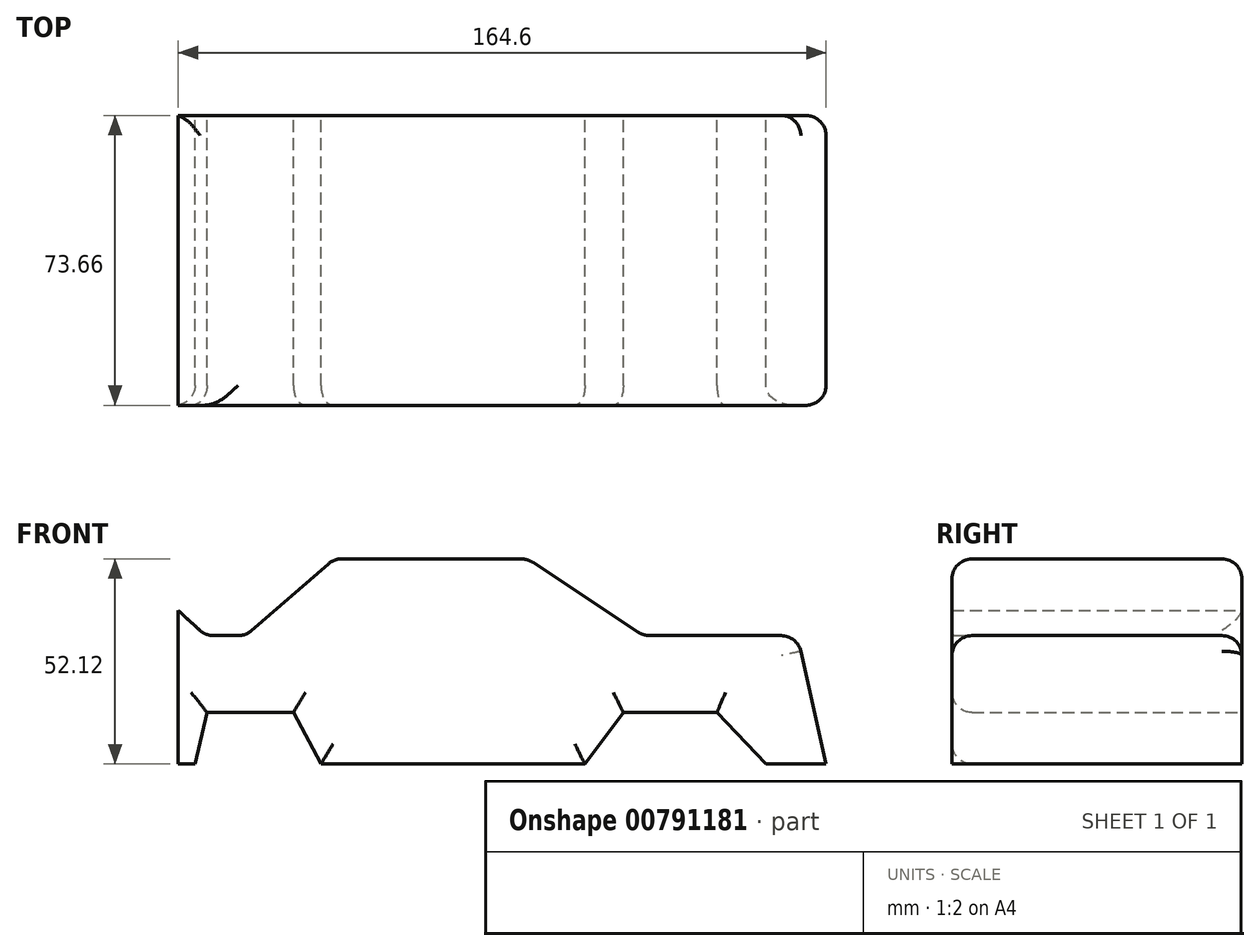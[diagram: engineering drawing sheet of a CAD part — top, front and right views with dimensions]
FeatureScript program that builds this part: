
annotation { "Feature Type Name" : "Feature", "Feature Type Description" : "" }
export const myFeature = defineFeature(function(context is Context, id is Id, definition is map)
    precondition{}
    {
        {
            var Q0;
            Q0=qCreatedBy(makeId("Front.planeOp"),FACE);
            var sketch = newSketch(context, id + "F0", { "sketchPlane" : qUnion([Q0])});
            skLineSegment(sketch, "E0", {"start": v(-94.95, -16.46) * mm, "end": v(-94.95, 22.56) * mm});
            skLineSegment(sketch, "E1", {"start": v(-94.95, 22.56) * mm, "end": v(-87.93, 16.15) * mm});
            skLineSegment(sketch, "E2", {"start": v(-87.93, 16.15) * mm, "end": v(-77.88, 16.15) * mm});
            skLineSegment(sketch, "E3", {"start": v(-77.88, 16.15) * mm, "end": v(-55.32, 35.66) * mm});
            skLineSegment(sketch, "E4", {"start": v(-6.25, 35.66) * mm, "end": v(-55.32, 35.66) * mm});
            skLineSegment(sketch, "E5", {"start": v(-6.25, 35.66) * mm, "end": v(23.32, 16.15) * mm});
            skLineSegment(sketch, "E6", {"start": v(23.32, 16.15) * mm, "end": v(62.33, 16.15) * mm});
            skLineSegment(sketch, "E7", {"start": v(62.33, 16.15) * mm, "end": v(69.65, -16.46) * mm});
            skLineSegment(sketch, "E8", {"start": v(69.65, -16.46) * mm, "end": v(54.4, -16.46) * mm});
            skLineSegment(sketch, "E9", {"start": v(54.4, -16.46) * mm, "end": v(41.91, -3.35) * mm});
            skLineSegment(sketch, "E10", {"start": v(18.14, -3.35) * mm, "end": v(41.91, -3.35) * mm});
            skLineSegment(sketch, "E11", {"start": v(18.14, -3.35) * mm, "end": v(8.38, -16.46) * mm});
            skLineSegment(sketch, "E12", {"start": v(8.38, -16.46) * mm, "end": v(-58.67, -16.46) * mm});
            skLineSegment(sketch, "E13", {"start": v(-58.67, -16.46) * mm, "end": v(-65.68, -3.35) * mm});
            skLineSegment(sketch, "E14", {"start": v(-87.63, -3.35) * mm, "end": v(-65.68, -3.35) * mm});
            skLineSegment(sketch, "E15", {"start": v(-87.63, -3.35) * mm, "end": v(-90.68, -16.46) * mm});
            skLineSegment(sketch, "E16", {"start": v(-90.68, -16.46) * mm, "end": v(-94.95, -16.46) * mm});
            skSolve(sketch);
        }
        {
            var Q0;
            Q0=makeQuery(id+"F0.imprint","IMPRINT",FACE,{"disambiguationData":[TD([[makeQuery(id+"F0.imprint","IMPRINT",EDGE,{"derivedFrom":sQuery(id+"F0.wireOp",EDGE,"E0")}),-1.0]])]});
            extrude(context, id + "F1", {"entities" : qUnion([Q0]), "depth" : 73.66 * mm, "offsetDistance" : 25.4 * mm});
        }
        {
            var Q0;
            Q0=makeQuery(id+"F1.opExtrude","CAP_EDGE",EDGE,{"disambiguationData":[OSD([sQuery(id+"F0.wireOp",EDGE,"E7")])],"isStart":true});
            var Q1;
            Q1=makeQuery(id+"F1.opExtrude","SWEPT_EDGE",EDGE,{"disambiguationData":[OSD([sQuery(id+"F0.wireOp",EDGE,"E6"),sQuery(id+"F0.wireOp",EDGE,"E7")])]});
            var Q2;
            Q2=makeQuery(id+"F1.opExtrude","CAP_EDGE",EDGE,{"disambiguationData":[OSD([sQuery(id+"F0.wireOp",EDGE,"E7")])],"isStart":false});
            var Q3;
            Q3=makeQuery(id+"F1.opExtrude","CAP_EDGE",EDGE,{"disambiguationData":[OSD([sQuery(id+"F0.wireOp",EDGE,"E6")])],"isStart":true});
            var Q4;
            Q4=makeQuery(id+"F1.opExtrude","CAP_EDGE",EDGE,{"disambiguationData":[OSD([sQuery(id+"F0.wireOp",EDGE,"E5")])],"isStart":true});
            var Q5;
            Q5=makeQuery(id+"F1.opExtrude","SWEPT_EDGE",EDGE,{"disambiguationData":[OSD([sQuery(id+"F0.wireOp",EDGE,"E4"),sQuery(id+"F0.wireOp",EDGE,"E5")])]});
            var Q6;
            Q6=makeQuery(id+"F1.opExtrude","CAP_EDGE",EDGE,{"disambiguationData":[OSD([sQuery(id+"F0.wireOp",EDGE,"E5")])],"isStart":false});
            var Q7;
            Q7=makeQuery(id+"F1.opExtrude","CAP_EDGE",EDGE,{"disambiguationData":[OSD([sQuery(id+"F0.wireOp",EDGE,"E6")])],"isStart":false});
            var Q8;
            Q8=makeQuery(id+"F1.opExtrude","SWEPT_EDGE",EDGE,{"disambiguationData":[OSD([sQuery(id+"F0.wireOp",EDGE,"E5"),sQuery(id+"F0.wireOp",EDGE,"E6")])]});
            var Q9;
            Q9=makeQuery(id+"F1.opExtrude","CAP_EDGE",EDGE,{"disambiguationData":[OSD([sQuery(id+"F0.wireOp",EDGE,"E4")])],"isStart":true});
            var Q10;
            Q10=makeQuery(id+"F1.opExtrude","SWEPT_EDGE",EDGE,{"disambiguationData":[OSD([sQuery(id+"F0.wireOp",EDGE,"E3"),sQuery(id+"F0.wireOp",EDGE,"E4")])]});
            var Q11;
            Q11=makeQuery(id+"F1.opExtrude","CAP_EDGE",EDGE,{"disambiguationData":[OSD([sQuery(id+"F0.wireOp",EDGE,"E4")])],"isStart":false});
            var Q12;
            Q12=makeQuery(id+"F1.opExtrude","CAP_EDGE",EDGE,{"disambiguationData":[OSD([sQuery(id+"F0.wireOp",EDGE,"E3")])],"isStart":false});
            var Q13;
            Q13=makeQuery(id+"F1.opExtrude","SWEPT_EDGE",EDGE,{"disambiguationData":[OSD([sQuery(id+"F0.wireOp",EDGE,"E2"),sQuery(id+"F0.wireOp",EDGE,"E3")])]});
            var Q14;
            Q14=makeQuery(id+"F1.opExtrude","CAP_EDGE",EDGE,{"disambiguationData":[OSD([sQuery(id+"F0.wireOp",EDGE,"E3")])],"isStart":true});
            var Q15;
            Q15=makeQuery(id+"F1.opExtrude","CAP_EDGE",EDGE,{"disambiguationData":[OSD([sQuery(id+"F0.wireOp",EDGE,"E2")])],"isStart":true});
            var Q16;
            Q16=makeQuery(id+"F1.opExtrude","SWEPT_EDGE",EDGE,{"disambiguationData":[OSD([sQuery(id+"F0.wireOp",EDGE,"E1"),sQuery(id+"F0.wireOp",EDGE,"E2")])]});
            var Q17;
            Q17=makeQuery(id+"F1.opExtrude","CAP_EDGE",EDGE,{"disambiguationData":[OSD([sQuery(id+"F0.wireOp",EDGE,"E15")])],"isStart":false});
            var Q18;
            Q18=makeQuery(id+"F1.opExtrude","CAP_EDGE",EDGE,{"disambiguationData":[OSD([sQuery(id+"F0.wireOp",EDGE,"E14")])],"isStart":false});
            var Q19;
            Q19=makeQuery(id+"F1.opExtrude","CAP_EDGE",EDGE,{"disambiguationData":[OSD([sQuery(id+"F0.wireOp",EDGE,"E13")])],"isStart":false});
            var Q20;
            Q20=makeQuery(id+"F1.opExtrude","CAP_EDGE",EDGE,{"disambiguationData":[OSD([sQuery(id+"F0.wireOp",EDGE,"E12")])],"isStart":false});
            var Q21;
            Q21=makeQuery(id+"F1.opExtrude","CAP_EDGE",EDGE,{"disambiguationData":[OSD([sQuery(id+"F0.wireOp",EDGE,"E11")])],"isStart":false});
            var Q22;
            Q22=makeQuery(id+"F1.opExtrude","CAP_EDGE",EDGE,{"disambiguationData":[OSD([sQuery(id+"F0.wireOp",EDGE,"E10")])],"isStart":false});
            var Q23;
            Q23=makeQuery(id+"F1.opExtrude","CAP_EDGE",EDGE,{"disambiguationData":[OSD([sQuery(id+"F0.wireOp",EDGE,"E9")])],"isStart":false});
            fillet(context, id + "F2", {"entities" : qUnion([Q0, Q1, Q2, Q3, Q4, Q5, Q6, Q7, Q8, Q9, Q10, Q11, Q12, Q13, Q14, Q15, Q16, Q17, Q18, Q19, Q20, Q21, Q22, Q23]), "radius" : 5.08 * mm, "tangentPropagation" : true, "allowEdgeOverflow" : false});
        }
    });
